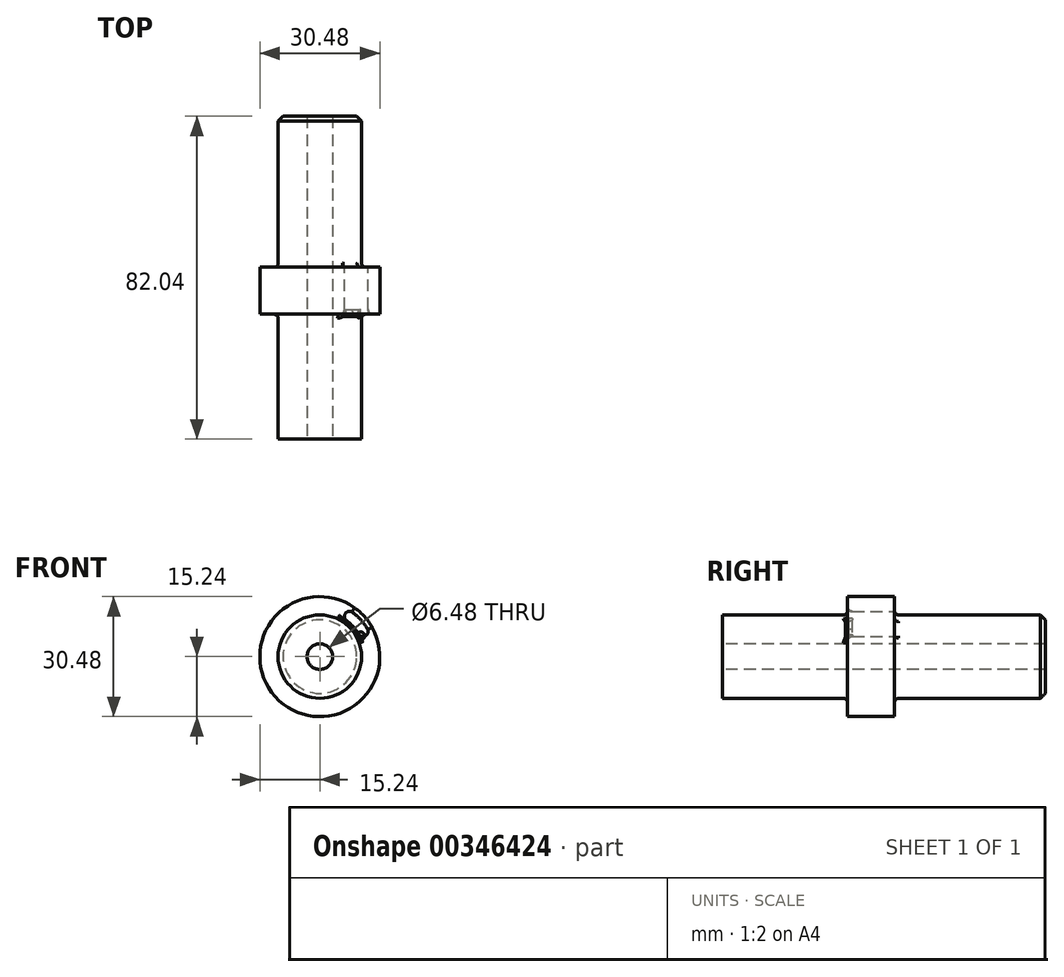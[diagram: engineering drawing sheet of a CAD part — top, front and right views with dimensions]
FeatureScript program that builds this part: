
annotation { "Feature Type Name" : "Feature", "Feature Type Description" : "" }
export const myFeature = defineFeature(function(context is Context, id is Id, definition is map)
    precondition{}
    {
        {
            var Q0;
            Q0=qCreatedBy(makeId("Front.planeOp"),FACE);
            var sketch = newSketch(context, id + "F0", { "sketchPlane" : qUnion([Q0])});
            skCircle(sketch, "E0", {"center": v(0, 15.24) * mm, "radius": 15.24 * mm});
            skSolve(sketch);
        }
        {
            var Q0;
            Q0=qSketchRegion(id+"F0",true);
            extrude(context, id + "F1", {"entities" : qUnion([Q0]), "depth" : 80 * mm});
        }
        {
            var Q0;
            Q0=makeQuery(id+"F1.opExtrude","CAP_FACE",FACE,{"disambiguationData":[OSD([sQuery(id+"F0.wireOp",EDGE,"E0")])],"isStart":false});
            var sketch = newSketch(context, id + "F2", { "sketchPlane" : qUnion([Q0])});
            skCircle(sketch, "E1", {"center": v(0, 15.24) * mm, "radius": 10.6 * mm});
            skSolve(sketch);
        }
        {
            var Q0;
            Q0=makeQuery(id+"F2.imprint","IMPRINT",FACE,{"disambiguationData":[TD([[makeQuery(id+"F2.imprint","IMPRINT",EDGE,{"derivedFrom":sQuery(id+"F2.wireOp",EDGE,"E1")}),-1.0]])]});
            extrude(context, id + "F3", {"entities" : qUnion([Q0]), "operationType" : NewBodyOperationType.REMOVE, "oppositeDirection" : true, "depth" : 34.04 * mm});
        }
        {
            var Q0;
            Q0=makeQuery(id+"F1.opExtrude","CAP_FACE",FACE,{"disambiguationData":[OSD([sQuery(id+"F0.wireOp",EDGE,"E0")])],"isStart":true});
            var sketch = newSketch(context, id + "F4", { "sketchPlane" : qUnion([Q0])});
            skCircle(sketch, "E2", {"center": v(0, 15.24) * mm, "radius": 10.6 * mm});
            skSolve(sketch);
        }
        {
            var Q0;
            Q0=makeQuery(id+"F4.imprint","IMPRINT",FACE,{"disambiguationData":[TD([[makeQuery(id+"F4.imprint","IMPRINT",EDGE,{"derivedFrom":sQuery(id+"F4.wireOp",EDGE,"E2")}),-1.0]])]});
            extrude(context, id + "F5", {"entities" : qUnion([Q0]), "operationType" : NewBodyOperationType.REMOVE, "oppositeDirection" : true, "depth" : 34.04 * mm});
        }
        {
            var Q0;
            Q0=makeQuery(id+"F5.boolean.opBoolean","COPY",FACE,{"derivedFrom":makeQuery(id+"F5.opExtrude","CAP_FACE",FACE,{"disambiguationData":[OSD([sQuery(id+"F0.wireOp",EDGE,"E0"),sQuery(id+"F4.wireOp",EDGE,"E2")])],"isStart":false})});
            var sketch = newSketch(context, id + "F6", { "sketchPlane" : qUnion([Q0])});
            skCircle(sketch, "E3.0", {"center": v(0, 15.24) * mm, "radius": 10.6 * mm});
            skArc(sketch, "E4.0", {"start": v(-1.24, 0.05) * mm, "mid": v(0, 0) * mm, "end": v(1.24, 0.05) * mm});
            skLineSegment(sketch, "E5", {"start": v(-10.6, 14.93) * mm, "end": v(-15.24, 14.93) * mm});
            skLineSegment(sketch, "E6", {"start": v(0, 15.24) * mm, "end": v(-13.88, 21.53) * mm});
            skLineSegment(sketch, "E7", {"start": v(0, 15.24) * mm, "end": v(-7.76, 28.35) * mm});
            skLineSegment(sketch, "E8", {"start": v(-12.73, 21) * mm, "end": v(-7.12, 27.26) * mm});
            skArc(sketch, "E9", {"start": v(-7.12, 27.26) * mm, "mid": v(-10.42, 24.58) * mm, "end": v(-12.73, 21) * mm});
            skLineSegment(sketch, "E10", {"start": v(-10.41, 19.96) * mm, "end": v(-5.82, 25.08) * mm});
            skArc(sketch, "E11", {"start": v(-5.82, 25.08) * mm, "mid": v(-8.45, 22.81) * mm, "end": v(-10.41, 19.96) * mm});
            skSolve(sketch);
        }
        {
            var Q0;
            {var subQ1=sQuery(id+"F6.wireOp",EDGE,"E8");Q0=makeQuery(id+"F6.imprint","IMPRINT",FACE,{"disambiguationData":[TD([[makeQuery(id+"F6.imprint","IMPRINT",EDGE,{"derivedFrom":subQ1}),-1.0]])]});}
            var Q1;
            Q1=makeQuery(id+"F6.imprint","IMPRINT",FACE,{"disambiguationData":[TD([[makeQuery(id+"F6.imprint","IMPRINT",EDGE,{"derivedFrom":sQuery(id+"F6.wireOp",EDGE,"E8")}),1.0]])]});
            extrude(context, id + "F7", {"entities" : qUnion([Q0, Q1]), "operationType" : NewBodyOperationType.REMOVE, "oppositeDirection" : true, "depth" : 25.4 * mm});
        }
        {
            var Q0;
            Q0=makeQuery(id+"F7.boolean.opBoolean","COPY",EDGE,{"derivedFrom":makeQuery(id+"F7.opExtrude","SWEPT_EDGE",EDGE,{"disambiguationData":[OSD([sQuery(id+"F6.wireOp",EDGE,"E6"),sQuery(id+"F6.wireOp",EDGE,"E10"),sQuery(id+"F6.wireOp",EDGE,"E11")])]})});
            var Q1;
            Q1=makeQuery(id+"F7.boolean.opBoolean","COPY",EDGE,{"derivedFrom":makeQuery(id+"F7.opExtrude","SWEPT_EDGE",EDGE,{"disambiguationData":[OSD([sQuery(id+"F6.wireOp",EDGE,"E7"),sQuery(id+"F6.wireOp",EDGE,"E10"),sQuery(id+"F6.wireOp",EDGE,"E11")])]})});
            var Q2;
            Q2=makeQuery(id+"F7.boolean.opBoolean","COPY",EDGE,{"derivedFrom":makeQuery(id+"F7.opExtrude","SWEPT_EDGE",EDGE,{"disambiguationData":[OSD([sQuery(id+"F6.wireOp",EDGE,"E6"),sQuery(id+"F6.wireOp",EDGE,"E8"),sQuery(id+"F6.wireOp",EDGE,"E9")])]})});
            var Q3;
            Q3=makeQuery(id+"F7.boolean.opBoolean","COPY",EDGE,{"derivedFrom":makeQuery(id+"F7.opExtrude","SWEPT_EDGE",EDGE,{"disambiguationData":[OSD([sQuery(id+"F6.wireOp",EDGE,"E7"),sQuery(id+"F6.wireOp",EDGE,"E8"),sQuery(id+"F6.wireOp",EDGE,"E9")])]})});
            fillet(context, id + "F8", {"entities" : qUnion([Q0, Q1, Q2, Q3]), "radius" : 1.27 * mm, "tangentPropagation" : true, "allowEdgeOverflow" : false});
        }
        {
            var Q0;
            Q0=makeQuery(id+"F5.boolean.opBoolean","COPY",EDGE,{"derivedFrom":makeQuery(id+"F5.opExtrude","CAP_EDGE",EDGE,{"disambiguationData":[OSD([sQuery(id+"F0.wireOp",EDGE,"E0")])],"isStart":false})});
            var Q1;
            Q1=makeQuery(id+"F3.boolean.opBoolean","COPY",EDGE,{"derivedFrom":makeQuery(id+"F3.opExtrude","CAP_EDGE",EDGE,{"disambiguationData":[OSD([sQuery(id+"F0.wireOp",EDGE,"E0")])],"isStart":false})});
            var Q2;
            Q2=makeQuery(id+"F8.opFillet","BLEND_EDGE",EDGE,{"blendedFrom":[makeQuery(id+"F7.boolean.opBoolean","COPY",EDGE,{"derivedFrom":makeQuery(id+"F7.opExtrude","SWEPT_EDGE",EDGE,{"disambiguationData":[OSD([sQuery(id+"F6.wireOp",EDGE,"E7"),sQuery(id+"F6.wireOp",EDGE,"E8"),sQuery(id+"F6.wireOp",EDGE,"E9")])]})}),makeQuery(id+"F3.boolean.opBoolean","COPY",FACE,{"derivedFrom":makeQuery(id+"F3.opExtrude","CAP_FACE",FACE,{"disambiguationData":[OSD([sQuery(id+"F0.wireOp",EDGE,"E0"),sQuery(id+"F2.wireOp",EDGE,"E1")])],"isStart":false})})],"blendedInto":[makeQuery(id+"F3.boolean.opBoolean","COPY",FACE,{"derivedFrom":makeQuery(id+"F3.opExtrude","CAP_FACE",FACE,{"disambiguationData":[OSD([sQuery(id+"F0.wireOp",EDGE,"E0"),sQuery(id+"F2.wireOp",EDGE,"E1")])],"isStart":false})})]});
            var Q3;
            Q3=makeQuery(id+"F8.opFillet","BLEND_EDGE",EDGE,{"blendedFrom":[makeQuery(id+"F7.boolean.opBoolean","COPY",EDGE,{"derivedFrom":makeQuery(id+"F7.opExtrude","SWEPT_EDGE",EDGE,{"disambiguationData":[OSD([sQuery(id+"F6.wireOp",EDGE,"E6"),sQuery(id+"F6.wireOp",EDGE,"E10"),sQuery(id+"F6.wireOp",EDGE,"E11")])]})}),makeQuery(id+"F3.boolean.opBoolean","COPY",FACE,{"derivedFrom":makeQuery(id+"F3.opExtrude","CAP_FACE",FACE,{"disambiguationData":[OSD([sQuery(id+"F0.wireOp",EDGE,"E0"),sQuery(id+"F2.wireOp",EDGE,"E1")])],"isStart":false})})],"blendedInto":[makeQuery(id+"F3.boolean.opBoolean","COPY",FACE,{"derivedFrom":makeQuery(id+"F3.opExtrude","CAP_FACE",FACE,{"disambiguationData":[OSD([sQuery(id+"F0.wireOp",EDGE,"E0"),sQuery(id+"F2.wireOp",EDGE,"E1")])],"isStart":false})})]});
            var Q4;
            Q4=makeQuery(id+"F8.opFillet","BLEND_EDGE",EDGE,{"blendedFrom":[makeQuery(id+"F7.boolean.opBoolean","COPY",EDGE,{"derivedFrom":makeQuery(id+"F7.opExtrude","SWEPT_EDGE",EDGE,{"disambiguationData":[OSD([sQuery(id+"F6.wireOp",EDGE,"E6"),sQuery(id+"F6.wireOp",EDGE,"E8"),sQuery(id+"F6.wireOp",EDGE,"E9")])]})}),makeQuery(id+"F3.boolean.opBoolean","COPY",FACE,{"derivedFrom":makeQuery(id+"F3.opExtrude","CAP_FACE",FACE,{"disambiguationData":[OSD([sQuery(id+"F0.wireOp",EDGE,"E0"),sQuery(id+"F2.wireOp",EDGE,"E1")])],"isStart":false})})],"blendedInto":[makeQuery(id+"F3.boolean.opBoolean","COPY",FACE,{"derivedFrom":makeQuery(id+"F3.opExtrude","CAP_FACE",FACE,{"disambiguationData":[OSD([sQuery(id+"F0.wireOp",EDGE,"E0"),sQuery(id+"F2.wireOp",EDGE,"E1")])],"isStart":false})})]});
            var Q5;
            Q5=makeQuery(id+"F8.opFillet","BLEND_EDGE",EDGE,{"blendedFrom":[makeQuery(id+"F7.boolean.opBoolean","COPY",EDGE,{"derivedFrom":makeQuery(id+"F7.opExtrude","SWEPT_EDGE",EDGE,{"disambiguationData":[OSD([sQuery(id+"F6.wireOp",EDGE,"E7"),sQuery(id+"F6.wireOp",EDGE,"E10"),sQuery(id+"F6.wireOp",EDGE,"E11")])]})}),makeQuery(id+"F3.boolean.opBoolean","COPY",FACE,{"derivedFrom":makeQuery(id+"F3.opExtrude","CAP_FACE",FACE,{"disambiguationData":[OSD([sQuery(id+"F0.wireOp",EDGE,"E0"),sQuery(id+"F2.wireOp",EDGE,"E1")])],"isStart":false})})],"blendedInto":[makeQuery(id+"F3.boolean.opBoolean","COPY",FACE,{"derivedFrom":makeQuery(id+"F3.opExtrude","CAP_FACE",FACE,{"disambiguationData":[OSD([sQuery(id+"F0.wireOp",EDGE,"E0"),sQuery(id+"F2.wireOp",EDGE,"E1")])],"isStart":false})})]});
            var Q6;
            Q6=makeQuery(id+"F7.boolean.opBoolean","INTERSECT",EDGE,{"derivedFrom":[makeQuery(id+"F3.boolean.opBoolean","COPY",FACE,{"derivedFrom":makeQuery(id+"F3.opExtrude","CAP_FACE",FACE,{"disambiguationData":[OSD([sQuery(id+"F0.wireOp",EDGE,"E0"),sQuery(id+"F2.wireOp",EDGE,"E1")])],"isStart":false})}),makeQuery(id+"F7.opExtrude","SWEPT_FACE",FACE,{"disambiguationData":[OSD([sQuery(id+"F6.wireOp",EDGE,"E11")])]})]});
            var Q7;
            Q7=makeQuery(id+"F7.boolean.opBoolean","INTERSECT",EDGE,{"derivedFrom":[makeQuery(id+"F3.boolean.opBoolean","COPY",FACE,{"derivedFrom":makeQuery(id+"F3.opExtrude","CAP_FACE",FACE,{"disambiguationData":[OSD([sQuery(id+"F0.wireOp",EDGE,"E0"),sQuery(id+"F2.wireOp",EDGE,"E1")])],"isStart":false})}),makeQuery(id+"F7.opExtrude","SWEPT_FACE",FACE,{"disambiguationData":[OSD([sQuery(id+"F6.wireOp",EDGE,"E9")])]})]});
            var Q8;
            Q8=makeQuery(id+"F7.boolean.opBoolean","COPY",EDGE,{"derivedFrom":makeQuery(id+"F7.opExtrude","CAP_EDGE",EDGE,{"disambiguationData":[OSD([sQuery(id+"F6.wireOp",EDGE,"E11")])],"isStart":true})});
            fillet(context, id + "F9", {"entities" : qUnion([Q0, Q1, Q2, Q3, Q4, Q5, Q6, Q7, Q8]), "radius" : 1.27 * mm, "tangentPropagation" : true, "allowEdgeOverflow" : false});
        }
        {
            var Q0;
            Q0=makeQuery(id+"F5.boolean.opBoolean","COPY",EDGE,{"derivedFrom":makeQuery(id+"F5.opExtrude","CAP_EDGE",EDGE,{"disambiguationData":[OSD([sQuery(id+"F4.wireOp",EDGE,"E2")])],"isStart":false})});
            var Q1;
            Q1=makeQuery(id+"F3.boolean.opBoolean","COPY",EDGE,{"derivedFrom":makeQuery(id+"F3.opExtrude","CAP_EDGE",EDGE,{"disambiguationData":[OSD([sQuery(id+"F2.wireOp",EDGE,"E1")])],"isStart":false})});
            fillet(context, id + "F10", {"entities" : qUnion([Q0, Q1]), "radius" : 1.02 * mm, "tangentPropagation" : true, "allowEdgeOverflow" : false});
        }
        {
            var Q0;
            Q0=makeQuery(id+"F1.opExtrude","CAP_FACE",FACE,{"disambiguationData":[OSD([sQuery(id+"F0.wireOp",EDGE,"E0")])],"isStart":true});
            extrude(context, id + "F11", {"entities" : qUnion([Q0]), "operationType" : NewBodyOperationType.ADD, "depth" : 4.32 * mm});
        }
        {
            var Q0;
            Q0=makeQuery(id+"F1.opExtrude","CAP_FACE",FACE,{"disambiguationData":[OSD([sQuery(id+"F0.wireOp",EDGE,"E0")])],"isStart":false});
            extrude(context, id + "F12", {"entities" : qUnion([Q0]), "operationType" : NewBodyOperationType.REMOVE, "oppositeDirection" : true, "depth" : 2.3 * mm});
        }
        {
            var Q0;
            Q0=makeQuery(id+"F12.boolean.opBoolean","COPY",EDGE,{"derivedFrom":makeQuery(id+"F12.opExtrude","CAP_EDGE",EDGE,{"disambiguationData":[OSD([sQuery(id+"F2.wireOp",EDGE,"E1")])],"isStart":false})});
            var Q1;
            Q1=makeQuery(id+"F11.opExtrude","CAP_EDGE",EDGE,{"disambiguationData":[OSD([sQuery(id+"F4.wireOp",EDGE,"E2")])],"isStart":false});
            chamfer(context, id + "F13", {"entities" : qUnion([Q0, Q1]), "width" : 1.27 * mm, "tangentPropagation" : true});
        }
        {
            var Q0;
            Q0=makeQuery(id+"F12.boolean.opBoolean","COPY",FACE,{"derivedFrom":makeQuery(id+"F12.opExtrude","CAP_FACE",FACE,{"disambiguationData":[OSD([sQuery(id+"F0.wireOp",EDGE,"E0")])],"isStart":false})});
            var sketch = newSketch(context, id + "F14", { "sketchPlane" : qUnion([Q0])});
            skCircle(sketch, "E12", {"center": v(0, 15.24) * mm, "radius": 3.24 * mm});
            skSolve(sketch);
        }
        {
            var Q0;
            Q0 = qSketchRegion(id + "F14", true);
            extrude(context, id + "F15", {"entities" : qUnion([Q0]), "operationType" : NewBodyOperationType.REMOVE, "endBound" : BoundingType.UP_TO_NEXT, "oppositeDirection" : true, "depth" : 25.4 * mm});
        }
    });
